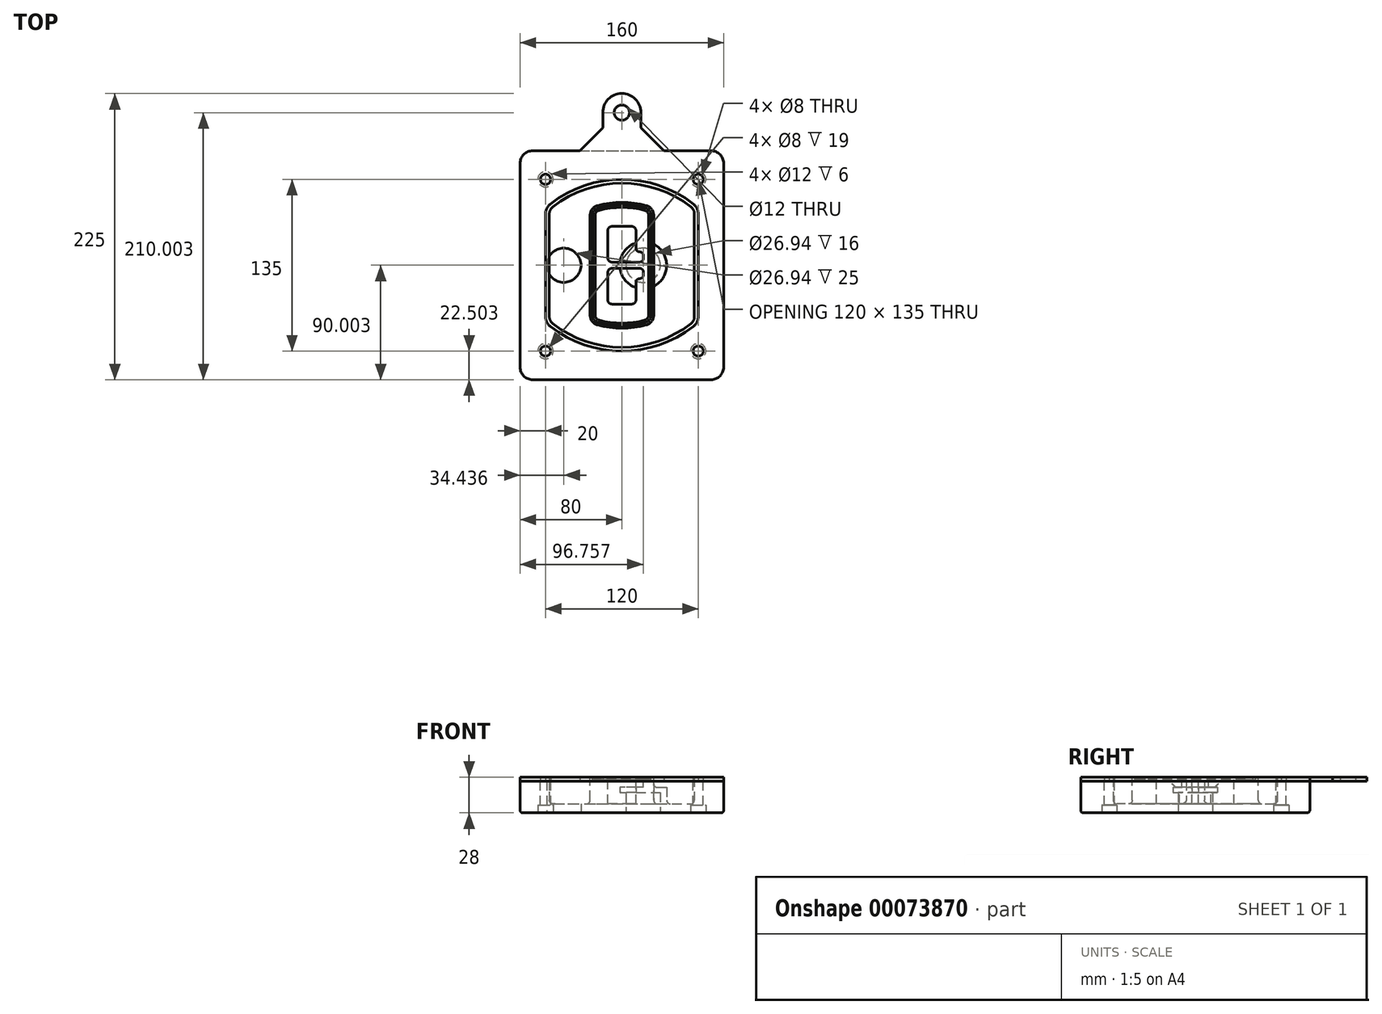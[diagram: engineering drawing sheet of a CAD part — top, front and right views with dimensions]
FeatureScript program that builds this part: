
annotation { "Feature Type Name" : "Feature", "Feature Type Description" : "" }
export const myFeature = defineFeature(function(context is Context, id is Id, definition is map)
    precondition{}
    {
        {
            var Q0;
            Q0=qCreatedBy(makeId("Top.planeOp"),FACE);
            var sketch = newSketch(context, id + "F0", { "sketchPlane" : qUnion([Q0])});
            skPoint(sketch, "E0.rect.middle", {"position": v(0, 0) * mm});
            skLineSegment(sketch, "E1.bottom", {"start": v(24.05, 28.38) * mm, "end": v(164.05, 28.38) * mm});
            skLineSegment(sketch, "E1.top", {"start": v(24.05, 208.38) * mm, "end": v(164.05, 208.38) * mm});
            skLineSegment(sketch, "E1.left", {"start": v(14.05, 38.38) * mm, "end": v(14.05, 198.38) * mm});
            skLineSegment(sketch, "E1.right", {"start": v(174.05, 38.38) * mm, "end": v(174.05, 198.38) * mm});
            skLineSegment(sketch, "E2", {"start": v(14.05, 208.38) * mm, "end": v(174.05, 28.38) * mm, "construction": true});
            skLineSegment(sketch, "E3", {"start": v(174.05, 208.38) * mm, "end": v(14.05, 28.38) * mm, "construction": true});
            skCircle(sketch, "E4", {"center": v(34.05, 185.88) * mm, "radius": 4 * mm});
            skCircle(sketch, "E5", {"center": v(154.05, 185.88) * mm, "radius": 4 * mm});
            skCircle(sketch, "E6", {"center": v(154.05, 50.88) * mm, "radius": 4 * mm});
            skCircle(sketch, "E7", {"center": v(34.05, 50.88) * mm, "radius": 4 * mm});
            skLineSegment(sketch, "E8", {"start": v(34.05, 185.88) * mm, "end": v(154.05, 185.88) * mm, "construction": true});
            skLineSegment(sketch, "E9", {"start": v(154.05, 185.88) * mm, "end": v(154.05, 50.88) * mm, "construction": true});
            skLineSegment(sketch, "E10", {"start": v(154.05, 50.88) * mm, "end": v(34.05, 50.88) * mm, "construction": true});
            skLineSegment(sketch, "E11", {"start": v(34.05, 50.88) * mm, "end": v(34.05, 185.88) * mm, "construction": true});
            skLineSegment(sketch, "E12", {"start": v(34.05, 158.68) * mm, "end": v(34.05, 78.09) * mm});
            skLineSegment(sketch, "E13", {"start": v(154.05, 158.68) * mm, "end": v(154.05, 78.09) * mm});
            skArc(sketch, "E14", {"start": v(150.2, 166.56) * mm, "mid": v(94.05, 185.88) * mm, "end": v(37.9, 166.56) * mm});
            skArc(sketch, "E15", {"start": v(37.9, 70.2) * mm, "mid": v(94.05, 50.88) * mm, "end": v(150.2, 70.2) * mm});
            skLineSegment(sketch, "E16", {"start": v(34.05, 118.38) * mm, "end": v(154.05, 118.38) * mm, "construction": true});
            skPoint(sketch, "E17.visualSharp", {"position": v(34.05, 73.38) * mm});
            skArc(sketch, "E17.filletArc", {"start": v(34.05, 78.09) * mm, "mid": v(35.06, 73.7) * mm, "end": v(37.9, 70.2) * mm});
            skPoint(sketch, "E18.visualSharp", {"position": v(34.05, 163.38) * mm});
            skArc(sketch, "E18.filletArc", {"start": v(37.9, 166.56) * mm, "mid": v(35.06, 163.06) * mm, "end": v(34.05, 158.68) * mm});
            skPoint(sketch, "E19.visualSharp", {"position": v(154.05, 163.38) * mm});
            skArc(sketch, "E19.filletArc", {"start": v(154.05, 158.68) * mm, "mid": v(153.04, 163.06) * mm, "end": v(150.2, 166.56) * mm});
            skPoint(sketch, "E20.visualSharp", {"position": v(154.05, 73.38) * mm});
            skArc(sketch, "E20.filletArc", {"start": v(150.2, 70.2) * mm, "mid": v(153.04, 73.7) * mm, "end": v(154.05, 78.09) * mm});
            skPoint(sketch, "E21.visualSharp", {"position": v(14.05, 208.38) * mm});
            skArc(sketch, "E21.filletArc", {"start": v(24.05, 208.38) * mm, "mid": v(16.98, 205.45) * mm, "end": v(14.05, 198.38) * mm});
            skPoint(sketch, "E22.visualSharp", {"position": v(174.05, 208.38) * mm});
            skArc(sketch, "E22.filletArc", {"start": v(174.05, 198.38) * mm, "mid": v(171.12, 205.45) * mm, "end": v(164.05, 208.38) * mm});
            skPoint(sketch, "E23.visualSharp", {"position": v(174.05, 28.38) * mm});
            skArc(sketch, "E23.filletArc", {"start": v(164.05, 28.38) * mm, "mid": v(171.12, 31.31) * mm, "end": v(174.05, 38.38) * mm});
            skPoint(sketch, "E24.visualSharp", {"position": v(14.05, 28.38) * mm});
            skArc(sketch, "E24.filletArc", {"start": v(14.05, 38.38) * mm, "mid": v(16.98, 31.31) * mm, "end": v(24.05, 28.38) * mm});
            skArc(sketch, "E25.0", {"start": v(151.05, 158.68) * mm, "mid": v(150.34, 161.75) * mm, "end": v(148.36, 164.2) * mm});
            skLineSegment(sketch, "E25.1", {"start": v(151.05, 158.68) * mm, "end": v(151.05, 78.09) * mm});
            skArc(sketch, "E25.2", {"start": v(148.36, 72.57) * mm, "mid": v(150.34, 75.02) * mm, "end": v(151.05, 78.09) * mm});
            skArc(sketch, "E25.3", {"start": v(39.74, 72.57) * mm, "mid": v(94.05, 53.88) * mm, "end": v(148.36, 72.57) * mm});
            skArc(sketch, "E25.4", {"start": v(37.05, 78.09) * mm, "mid": v(37.76, 75.02) * mm, "end": v(39.74, 72.57) * mm});
            skArc(sketch, "E25.5", {"start": v(148.36, 164.2) * mm, "mid": v(94.05, 182.88) * mm, "end": v(39.74, 164.2) * mm});
            skLineSegment(sketch, "E25.6", {"start": v(37.05, 158.68) * mm, "end": v(37.05, 78.09) * mm});
            skArc(sketch, "E25.7", {"start": v(39.74, 164.2) * mm, "mid": v(37.76, 161.75) * mm, "end": v(37.05, 158.68) * mm});
            skArc(sketch, "E26.0", {"start": v(35.43, 169.71) * mm, "mid": v(31.47, 164.82) * mm, "end": v(30.05, 158.68) * mm});
            skArc(sketch, "E26.1", {"start": v(152.67, 169.71) * mm, "mid": v(94.05, 189.88) * mm, "end": v(35.43, 169.71) * mm});
            skArc(sketch, "E26.2", {"start": v(158.05, 158.68) * mm, "mid": v(156.63, 164.82) * mm, "end": v(152.67, 169.71) * mm});
            skLineSegment(sketch, "E26.3", {"start": v(158.05, 158.68) * mm, "end": v(158.05, 78.09) * mm});
            skArc(sketch, "E26.4", {"start": v(152.67, 67.05) * mm, "mid": v(156.63, 71.95) * mm, "end": v(158.05, 78.09) * mm});
            skLineSegment(sketch, "E26.5", {"start": v(30.05, 158.68) * mm, "end": v(30.05, 78.09) * mm});
            skArc(sketch, "E26.6", {"start": v(35.43, 67.05) * mm, "mid": v(94.05, 46.88) * mm, "end": v(152.67, 67.05) * mm});
            skArc(sketch, "E26.7", {"start": v(30.05, 78.09) * mm, "mid": v(31.47, 71.95) * mm, "end": v(35.43, 67.05) * mm});
            skSolve(sketch);
        }
        {
            var Q0;
            Q0=makeQuery(id+"F0.imprint","IMPRINT",FACE,{"disambiguationData":[TD([[makeQuery(id+"F0.imprint","IMPRINT",EDGE,{"derivedFrom":sQuery(id+"F0.wireOp",EDGE,"E1.bottom")}),1.0]])]});
            var Q1;
            Q1=makeQuery(id+"F0.imprint","IMPRINT",FACE,{"disambiguationData":[TD([[makeQuery(id+"F0.imprint","IMPRINT",EDGE,{"derivedFrom":sQuery(id+"F0.wireOp",EDGE,"E12")}),1.0]])]});
            var Q2;
            Q2=makeQuery(id+"F0.imprint","IMPRINT",FACE,{"disambiguationData":[TD([[makeQuery(id+"F0.imprint","IMPRINT",EDGE,{"derivedFrom":sQuery(id+"F0.wireOp",EDGE,"E25.0")}),1.0]])]});
            var Q3;
            Q3=makeQuery(id+"F0.imprint","IMPRINT",FACE,{"disambiguationData":[TD([[makeQuery(id+"F0.imprint","IMPRINT",EDGE,{"derivedFrom":sQuery(id+"F0.wireOp",EDGE,"E12")}),-1.0]])]});
            extrude(context, id + "F1", {"entities" : qUnion([Q0, Q1, Q2, Q3]), "oppositeDirection" : true, "depth" : 25 * mm});
        }
        {
            var Q0;
            Q0=makeQuery(id+"F0.imprint","IMPRINT",FACE,{"disambiguationData":[TD([[makeQuery(id+"F0.imprint","IMPRINT",EDGE,{"derivedFrom":sQuery(id+"F0.wireOp",EDGE,"E12")}),1.0]])]});
            extrude(context, id + "F2", {"entities" : qUnion([Q0]), "operationType" : NewBodyOperationType.ADD, "depth" : 3 * mm});
        }
        {
            var Q0;
            Q0=makeQuery(id+"F0.imprint","IMPRINT",FACE,{"disambiguationData":[TD([[makeQuery(id+"F0.imprint","IMPRINT",EDGE,{"derivedFrom":sQuery(id+"F0.wireOp",EDGE,"E25.0")}),1.0]])]});
            extrude(context, id + "F3", {"entities" : qUnion([Q0]), "operationType" : NewBodyOperationType.REMOVE, "oppositeDirection" : true, "depth" : 18 * mm});
        }
        {
            var Q0;
            Q0=makeQuery(id+"F2.opExtrude","CAP_FACE",FACE,{"disambiguationData":[OSD([sQuery(id+"F0.wireOp",EDGE,"E12"),sQuery(id+"F0.wireOp",EDGE,"E13"),sQuery(id+"F0.wireOp",EDGE,"E14"),sQuery(id+"F0.wireOp",EDGE,"E15"),sQuery(id+"F0.wireOp",EDGE,"E17.filletArc"),sQuery(id+"F0.wireOp",EDGE,"E18.filletArc"),sQuery(id+"F0.wireOp",EDGE,"E19.filletArc"),sQuery(id+"F0.wireOp",EDGE,"E20.filletArc"),sQuery(id+"F0.wireOp",EDGE,"E25.0"),sQuery(id+"F0.wireOp",EDGE,"E25.1"),sQuery(id+"F0.wireOp",EDGE,"E25.2"),sQuery(id+"F0.wireOp",EDGE,"E25.3"),sQuery(id+"F0.wireOp",EDGE,"E25.4"),sQuery(id+"F0.wireOp",EDGE,"E25.5"),sQuery(id+"F0.wireOp",EDGE,"E25.6"),sQuery(id+"F0.wireOp",EDGE,"E25.7")])],"isStart":false});
            var sketch = newSketch(context, id + "F4", { "sketchPlane" : qUnion([Q0])});
            skArc(sketch, "E27.0", {"start": v(74.97, 71.41) * mm, "mid": v(94.05, 68.88) * mm, "end": v(113.13, 71.41) * mm});
            skArc(sketch, "E28.0", {"start": v(113.13, 165.35) * mm, "mid": v(94.05, 167.88) * mm, "end": v(74.97, 165.35) * mm});
            skLineSegment(sketch, "E29", {"start": v(69.05, 157.63) * mm, "end": v(69.05, 79.14) * mm});
            skLineSegment(sketch, "E30", {"start": v(119.05, 157.63) * mm, "end": v(119.05, 79.14) * mm});
            skLineSegment(sketch, "E31", {"start": v(69.05, 163.48) * mm, "end": v(119.05, 163.48) * mm, "construction": true});
            skLineSegment(sketch, "E32", {"start": v(69.05, 73.28) * mm, "end": v(119.05, 73.28) * mm, "construction": true});
            skPoint(sketch, "E33.visualSharp", {"position": v(69.05, 163.48) * mm});
            skArc(sketch, "E33.filletArc", {"start": v(74.97, 165.35) * mm, "mid": v(70.7, 162.5) * mm, "end": v(69.05, 157.63) * mm});
            skPoint(sketch, "E34.visualSharp", {"position": v(119.05, 163.48) * mm});
            skArc(sketch, "E34.filletArc", {"start": v(119.05, 157.63) * mm, "mid": v(117.4, 162.5) * mm, "end": v(113.13, 165.35) * mm});
            skPoint(sketch, "E35.visualSharp", {"position": v(119.05, 73.28) * mm});
            skArc(sketch, "E35.filletArc", {"start": v(113.13, 71.41) * mm, "mid": v(117.4, 74.27) * mm, "end": v(119.05, 79.14) * mm});
            skPoint(sketch, "E36.visualSharp", {"position": v(69.05, 73.28) * mm});
            skArc(sketch, "E36.filletArc", {"start": v(69.05, 79.14) * mm, "mid": v(70.7, 74.27) * mm, "end": v(74.97, 71.41) * mm});
            skArc(sketch, "E37.0", {"start": v(148.36, 164.2) * mm, "mid": v(94.05, 182.88) * mm, "end": v(39.74, 164.2) * mm});
            skArc(sketch, "E37.1", {"start": v(39.74, 164.2) * mm, "mid": v(37.76, 161.75) * mm, "end": v(37.05, 158.68) * mm});
            skLineSegment(sketch, "E37.2", {"start": v(37.05, 158.68) * mm, "end": v(37.05, 78.09) * mm});
            skArc(sketch, "E37.3", {"start": v(37.05, 78.09) * mm, "mid": v(37.76, 75.02) * mm, "end": v(39.74, 72.57) * mm});
            skArc(sketch, "E37.4", {"start": v(39.74, 72.57) * mm, "mid": v(94.05, 53.88) * mm, "end": v(148.36, 72.57) * mm});
            skArc(sketch, "E37.5", {"start": v(148.36, 72.57) * mm, "mid": v(150.34, 75.02) * mm, "end": v(151.05, 78.09) * mm});
            skLineSegment(sketch, "E37.6", {"start": v(151.05, 158.68) * mm, "end": v(151.05, 78.09) * mm});
            skArc(sketch, "E37.7", {"start": v(151.05, 158.68) * mm, "mid": v(150.34, 161.75) * mm, "end": v(148.36, 164.2) * mm});
            skLineSegment(sketch, "E38.0", {"start": v(117.05, 157.63) * mm, "end": v(117.05, 79.14) * mm});
            skArc(sketch, "E38.1", {"start": v(112.61, 73.34) * mm, "mid": v(115.81, 75.49) * mm, "end": v(117.05, 79.14) * mm});
            skArc(sketch, "E38.2", {"start": v(75.49, 73.34) * mm, "mid": v(94.05, 70.88) * mm, "end": v(112.61, 73.34) * mm});
            skArc(sketch, "E38.3", {"start": v(71.05, 79.14) * mm, "mid": v(72.29, 75.49) * mm, "end": v(75.49, 73.34) * mm});
            skLineSegment(sketch, "E38.4", {"start": v(71.05, 157.63) * mm, "end": v(71.05, 79.14) * mm});
            skArc(sketch, "E38.5", {"start": v(117.05, 157.63) * mm, "mid": v(115.81, 161.28) * mm, "end": v(112.61, 163.42) * mm});
            skArc(sketch, "E38.6", {"start": v(75.49, 163.42) * mm, "mid": v(72.29, 161.28) * mm, "end": v(71.05, 157.63) * mm});
            skArc(sketch, "E38.7", {"start": v(112.61, 163.42) * mm, "mid": v(94.05, 165.88) * mm, "end": v(75.49, 163.42) * mm});
            skArc(sketch, "E39.0", {"start": v(115.05, 157.63) * mm, "mid": v(114.23, 160.06) * mm, "end": v(112.1, 161.5) * mm});
            skLineSegment(sketch, "E39.1", {"start": v(115.05, 157.63) * mm, "end": v(115.05, 79.14) * mm});
            skArc(sketch, "E39.2", {"start": v(112.1, 75.27) * mm, "mid": v(114.23, 76.7) * mm, "end": v(115.05, 79.14) * mm});
            skArc(sketch, "E39.3", {"start": v(76, 75.27) * mm, "mid": v(94.05, 72.88) * mm, "end": v(112.1, 75.27) * mm});
            skArc(sketch, "E39.4", {"start": v(73.05, 79.14) * mm, "mid": v(73.87, 76.7) * mm, "end": v(76, 75.27) * mm});
            skArc(sketch, "E39.5", {"start": v(112.1, 161.5) * mm, "mid": v(94.05, 163.88) * mm, "end": v(76, 161.5) * mm});
            skLineSegment(sketch, "E39.6", {"start": v(73.05, 157.63) * mm, "end": v(73.05, 79.14) * mm});
            skArc(sketch, "E39.7", {"start": v(76, 161.5) * mm, "mid": v(73.87, 160.06) * mm, "end": v(73.05, 157.63) * mm});
            skLineSegment(sketch, "E40", {"start": v(69.05, 118.38) * mm, "end": v(119.05, 118.38) * mm, "construction": true});
            skLineSegment(sketch, "E41", {"start": v(83.05, 123.88) * mm, "end": v(83.05, 145.88) * mm});
            skLineSegment(sketch, "E42", {"start": v(86.05, 148.88) * mm, "end": v(102.05, 148.88) * mm});
            skLineSegment(sketch, "E43", {"start": v(105.05, 145.88) * mm, "end": v(105.05, 131.88) * mm});
            skLineSegment(sketch, "E44", {"start": v(108.05, 128.88) * mm, "end": v(108.05, 128.88) * mm});
            skLineSegment(sketch, "E45", {"start": v(111.05, 125.88) * mm, "end": v(111.05, 123.88) * mm});
            skLineSegment(sketch, "E46", {"start": v(108.05, 120.88) * mm, "end": v(86.05, 120.88) * mm});
            skPoint(sketch, "E47.visualSharp", {"position": v(83.05, 148.88) * mm});
            skArc(sketch, "E47.filletArc", {"start": v(86.05, 148.88) * mm, "mid": v(83.93, 148) * mm, "end": v(83.05, 145.88) * mm});
            skPoint(sketch, "E48.visualSharp", {"position": v(105.05, 148.88) * mm});
            skArc(sketch, "E48.filletArc", {"start": v(105.05, 145.88) * mm, "mid": v(104.17, 148) * mm, "end": v(102.05, 148.88) * mm});
            skPoint(sketch, "E49.visualSharp", {"position": v(105.05, 128.88) * mm});
            skArc(sketch, "E49.filletArc", {"start": v(105.05, 131.88) * mm, "mid": v(105.93, 129.76) * mm, "end": v(108.05, 128.88) * mm});
            skPoint(sketch, "E50.visualSharp", {"position": v(111.05, 128.88) * mm});
            skArc(sketch, "E50.filletArc", {"start": v(111.05, 125.88) * mm, "mid": v(110.17, 128) * mm, "end": v(108.05, 128.88) * mm});
            skPoint(sketch, "E51.visualSharp", {"position": v(111.05, 120.88) * mm});
            skArc(sketch, "E51.filletArc", {"start": v(108.05, 120.88) * mm, "mid": v(110.17, 121.76) * mm, "end": v(111.05, 123.88) * mm});
            skPoint(sketch, "E52.visualSharp", {"position": v(83.05, 120.88) * mm});
            skArc(sketch, "E52.filletArc", {"start": v(83.05, 123.88) * mm, "mid": v(83.93, 121.76) * mm, "end": v(86.05, 120.88) * mm});
            skLineSegment(sketch, "E53.0.MirrorCS", {"start": v(108.05, 115.88) * mm, "end": v(86.05, 115.88) * mm});
            skArc(sketch, "E54.0.MirrorCS", {"start": v(83.05, 112.88) * mm, "mid": v(83.93, 115) * mm, "end": v(86.05, 115.88) * mm});
            skLineSegment(sketch, "E55.0.MirrorCS", {"start": v(83.05, 112.88) * mm, "end": v(83.05, 90.88) * mm});
            skArc(sketch, "E56.0.MirrorCS", {"start": v(86.05, 87.88) * mm, "mid": v(83.93, 88.76) * mm, "end": v(83.05, 90.88) * mm});
            skLineSegment(sketch, "E57.0.MirrorCS", {"start": v(86.05, 87.88) * mm, "end": v(102.05, 87.88) * mm});
            skArc(sketch, "E58.0.MirrorCS", {"start": v(105.05, 90.88) * mm, "mid": v(104.17, 88.76) * mm, "end": v(102.05, 87.88) * mm});
            skLineSegment(sketch, "E59.0.MirrorCS", {"start": v(105.05, 90.88) * mm, "end": v(105.05, 104.88) * mm});
            skArc(sketch, "E60.0.MirrorCS", {"start": v(105.05, 104.88) * mm, "mid": v(105.93, 107) * mm, "end": v(108.05, 107.88) * mm});
            skArc(sketch, "E61.0.MirrorCS", {"start": v(111.05, 110.88) * mm, "mid": v(110.17, 108.76) * mm, "end": v(108.05, 107.88) * mm});
            skLineSegment(sketch, "E62.0.MirrorCS", {"start": v(111.05, 110.88) * mm, "end": v(111.05, 112.88) * mm});
            skArc(sketch, "E63.0.MirrorCS", {"start": v(108.05, 115.88) * mm, "mid": v(110.17, 115) * mm, "end": v(111.05, 112.88) * mm});
            skSolve(sketch);
        }
        {
            var Q0;
            Q0=makeQuery(id+"F4.imprint","IMPRINT",FACE,{"disambiguationData":[TD([[makeQuery(id+"F4.imprint","IMPRINT",EDGE,{"derivedFrom":sQuery(id+"F4.wireOp",EDGE,"E27.0")}),1.0]])]});
            var Q1;
            Q1=makeQuery(id+"F4.imprint","IMPRINT",FACE,{"disambiguationData":[TD([[makeQuery(id+"F4.imprint","IMPRINT",EDGE,{"derivedFrom":sQuery(id+"F4.wireOp",EDGE,"E38.0")}),-1.0]])]});
            var Q2;
            Q2=makeQuery(id+"F4.imprint","IMPRINT",FACE,{"disambiguationData":[TD([[makeQuery(id+"F4.imprint","IMPRINT",EDGE,{"derivedFrom":sQuery(id+"F4.wireOp",EDGE,"E39.0")}),1.0]])]});
            extrude(context, id + "F5", {"entities" : qUnion([Q0, Q1, Q2]), "operationType" : NewBodyOperationType.ADD, "endBound" : BoundingType.UP_TO_NEXT, "oppositeDirection" : true, "depth" : 25 * mm});
        }
        {
            var Q0;
            Q0=makeQuery(id+"F4.imprint","IMPRINT",FACE,{"disambiguationData":[TD([[makeQuery(id+"F4.imprint","IMPRINT",EDGE,{"derivedFrom":sQuery(id+"F4.wireOp",EDGE,"E38.0")}),-1.0]])]});
            extrude(context, id + "F6", {"entities" : qUnion([Q0]), "operationType" : NewBodyOperationType.REMOVE, "oppositeDirection" : true, "depth" : 2 * mm});
        }
        {
            var Q0;
            Q0=makeQuery(id+"F1.opExtrude","CAP_FACE",FACE,{"disambiguationData":[OSD([sQuery(id+"F0.wireOp",EDGE,"E1.bottom"),sQuery(id+"F0.wireOp",EDGE,"E1.top"),sQuery(id+"F0.wireOp",EDGE,"E1.left"),sQuery(id+"F0.wireOp",EDGE,"E1.right"),sQuery(id+"F0.wireOp",EDGE,"E4"),sQuery(id+"F0.wireOp",EDGE,"E5"),sQuery(id+"F0.wireOp",EDGE,"E6"),sQuery(id+"F0.wireOp",EDGE,"E7"),sQuery(id+"F0.wireOp",EDGE,"E21.filletArc"),sQuery(id+"F0.wireOp",EDGE,"E22.filletArc"),sQuery(id+"F0.wireOp",EDGE,"E23.filletArc"),sQuery(id+"F0.wireOp",EDGE,"E24.filletArc")])],"isStart":false});
            var sketch = newSketch(context, id + "F7", { "sketchPlane" : qUnion([Q0])});
            skCircle(sketch, "E64", {"center": v(110.8, -118.38) * mm, "radius": 13.47 * mm});
            skCircle(sketch, "E65", {"center": v(48.49, -118.38) * mm, "radius": 13.47 * mm});
            skLineSegment(sketch, "E66", {"start": v(174.05, -118.38) * mm, "end": v(14.05, -118.38) * mm});
            skCircle(sketch, "E67", {"center": v(110.8, -118.38) * mm, "radius": 18.47 * mm});
            skCircle(sketch, "E68", {"center": v(154.05, -185.88) * mm, "radius": 6 * mm});
            skCircle(sketch, "E69", {"center": v(34.05, -185.88) * mm, "radius": 6 * mm});
            skCircle(sketch, "E70", {"center": v(34.05, -50.88) * mm, "radius": 6 * mm});
            skCircle(sketch, "E71", {"center": v(154.05, -50.88) * mm, "radius": 6 * mm});
            skSolve(sketch);
        }
        {
            var Q0;
            {var subQ1=sQuery(id+"F7.wireOp",EDGE,"E66");var subQ4=sQuery(id+"F7.wireOp",EDGE,"E64");var subQ6=makeQuery(id+"F7.imprint","INTERSECT",VERTEX,{"disambiguationData":[OD(0.0)],"derivedFrom":[subQ4,subQ1]});Q0=makeQuery(id+"F7.imprint","IMPRINT",FACE,{"disambiguationData":[TD([[makeQuery(id+"F7.imprint","IMPRINT",EDGE,{"disambiguationData":[TD([[subQ6,-1.0]])],"derivedFrom":subQ4}),-1.0]])]});}
            var Q1;
            {var subQ0=sQuery(id+"F7.wireOp",EDGE,"E66");var subQ1=sQuery(id+"F7.wireOp",EDGE,"E64");var subQ3=makeQuery(id+"F7.imprint","INTERSECT",VERTEX,{"disambiguationData":[OD(0.0)],"derivedFrom":[subQ1,subQ0]});Q1=makeQuery(id+"F7.imprint","IMPRINT",FACE,{"disambiguationData":[TD([[makeQuery(id+"F7.imprint","IMPRINT",EDGE,{"disambiguationData":[TD([[subQ3,-1.0]])],"derivedFrom":subQ1}),1.0]])]});}
            var Q2;
            {var subQ0=sQuery(id+"F7.wireOp",EDGE,"E66");var subQ1=sQuery(id+"F7.wireOp",EDGE,"E64");var subQ3=makeQuery(id+"F7.imprint","INTERSECT",VERTEX,{"disambiguationData":[OD(0.0)],"derivedFrom":[subQ1,subQ0]});Q2=makeQuery(id+"F7.imprint","IMPRINT",FACE,{"disambiguationData":[TD([[makeQuery(id+"F7.imprint","IMPRINT",EDGE,{"disambiguationData":[TD([[subQ3,1.0]])],"derivedFrom":subQ1}),1.0]])]});}
            var Q3;
            {var subQ1=sQuery(id+"F7.wireOp",EDGE,"E66");var subQ4=sQuery(id+"F7.wireOp",EDGE,"E64");var subQ6=makeQuery(id+"F7.imprint","INTERSECT",VERTEX,{"disambiguationData":[OD(0.0)],"derivedFrom":[subQ4,subQ1]});Q3=makeQuery(id+"F7.imprint","IMPRINT",FACE,{"disambiguationData":[TD([[makeQuery(id+"F7.imprint","IMPRINT",EDGE,{"disambiguationData":[TD([[subQ6,1.0]])],"derivedFrom":subQ4}),-1.0]])]});}
            extrude(context, id + "F8", {"entities" : qUnion([Q0, Q1, Q2, Q3]), "operationType" : NewBodyOperationType.ADD, "oppositeDirection" : true, "depth" : 20 * mm});
        }
        {
            var Q0;
            {var subQ0=sQuery(id+"F7.wireOp",EDGE,"E66");var subQ1=sQuery(id+"F7.wireOp",EDGE,"E64");var subQ3=makeQuery(id+"F7.imprint","INTERSECT",VERTEX,{"disambiguationData":[OD(0.0)],"derivedFrom":[subQ1,subQ0]});Q0=makeQuery(id+"F7.imprint","IMPRINT",FACE,{"disambiguationData":[TD([[makeQuery(id+"F7.imprint","IMPRINT",EDGE,{"disambiguationData":[TD([[subQ3,-1.0]])],"derivedFrom":subQ1}),1.0]])]});}
            var Q1;
            {var subQ0=sQuery(id+"F7.wireOp",EDGE,"E66");var subQ1=sQuery(id+"F7.wireOp",EDGE,"E64");var subQ3=makeQuery(id+"F7.imprint","INTERSECT",VERTEX,{"disambiguationData":[OD(0.0)],"derivedFrom":[subQ1,subQ0]});Q1=makeQuery(id+"F7.imprint","IMPRINT",FACE,{"disambiguationData":[TD([[makeQuery(id+"F7.imprint","IMPRINT",EDGE,{"disambiguationData":[TD([[subQ3,1.0]])],"derivedFrom":subQ1}),1.0]])]});}
            extrude(context, id + "F9", {"entities" : qUnion([Q0, Q1]), "operationType" : NewBodyOperationType.REMOVE, "oppositeDirection" : true, "depth" : 16 * mm});
        }
        {
            var Q0;
            {var subQ0=sQuery(id+"F7.wireOp",EDGE,"E66");var subQ1=sQuery(id+"F7.wireOp",EDGE,"E65");var subQ3=makeQuery(id+"F7.imprint","INTERSECT",VERTEX,{"disambiguationData":[OD(0.0)],"derivedFrom":[subQ1,subQ0]});Q0=makeQuery(id+"F7.imprint","IMPRINT",FACE,{"disambiguationData":[TD([[makeQuery(id+"F7.imprint","IMPRINT",EDGE,{"disambiguationData":[TD([[subQ3,-1.0]])],"derivedFrom":subQ1}),1.0]])]});}
            var Q1;
            {var subQ0=sQuery(id+"F7.wireOp",EDGE,"E66");var subQ1=sQuery(id+"F7.wireOp",EDGE,"E65");var subQ3=makeQuery(id+"F7.imprint","INTERSECT",VERTEX,{"disambiguationData":[OD(0.0)],"derivedFrom":[subQ1,subQ0]});Q1=makeQuery(id+"F7.imprint","IMPRINT",FACE,{"disambiguationData":[TD([[makeQuery(id+"F7.imprint","IMPRINT",EDGE,{"disambiguationData":[TD([[subQ3,1.0]])],"derivedFrom":subQ1}),1.0]])]});}
            extrude(context, id + "F10", {"entities" : qUnion([Q0, Q1]), "operationType" : NewBodyOperationType.REMOVE, "oppositeDirection" : true, "depth" : 25 * mm});
        }
        {
            var Q0;
            Q0=makeQuery(id+"F7.imprint","IMPRINT",FACE,{"disambiguationData":[TD([[makeQuery(id+"F7.imprint","IMPRINT",EDGE,{"derivedFrom":sQuery(id+"F7.wireOp",EDGE,"E68")}),1.0]])]});
            var Q1;
            Q1=makeQuery(id+"F7.imprint","IMPRINT",FACE,{"disambiguationData":[TD([[makeQuery(id+"F7.imprint","IMPRINT",EDGE,{"derivedFrom":makeQuery(id+"F1.opExtrude","CAP_EDGE",EDGE,{"disambiguationData":[OSD([sQuery(id+"F0.wireOp",EDGE,"E5")])],"isStart":false})}),-1.0]])]});
            var Q2;
            Q2=makeQuery(id+"F7.imprint","IMPRINT",FACE,{"disambiguationData":[TD([[makeQuery(id+"F7.imprint","IMPRINT",EDGE,{"derivedFrom":sQuery(id+"F7.wireOp",EDGE,"E69")}),1.0]])]});
            var Q3;
            Q3=makeQuery(id+"F7.imprint","IMPRINT",FACE,{"disambiguationData":[TD([[makeQuery(id+"F7.imprint","IMPRINT",EDGE,{"derivedFrom":makeQuery(id+"F1.opExtrude","CAP_EDGE",EDGE,{"disambiguationData":[OSD([sQuery(id+"F0.wireOp",EDGE,"E4")])],"isStart":false})}),-1.0]])]});
            var Q4;
            Q4=makeQuery(id+"F7.imprint","IMPRINT",FACE,{"disambiguationData":[TD([[makeQuery(id+"F7.imprint","IMPRINT",EDGE,{"derivedFrom":sQuery(id+"F7.wireOp",EDGE,"E70")}),1.0]])]});
            var Q5;
            Q5=makeQuery(id+"F7.imprint","IMPRINT",FACE,{"disambiguationData":[TD([[makeQuery(id+"F7.imprint","IMPRINT",EDGE,{"derivedFrom":makeQuery(id+"F1.opExtrude","CAP_EDGE",EDGE,{"disambiguationData":[OSD([sQuery(id+"F0.wireOp",EDGE,"E7")])],"isStart":false})}),-1.0]])]});
            var Q6;
            Q6=makeQuery(id+"F7.imprint","IMPRINT",FACE,{"disambiguationData":[TD([[makeQuery(id+"F7.imprint","IMPRINT",EDGE,{"derivedFrom":sQuery(id+"F7.wireOp",EDGE,"E71")}),1.0]])]});
            var Q7;
            Q7=makeQuery(id+"F7.imprint","IMPRINT",FACE,{"disambiguationData":[TD([[makeQuery(id+"F7.imprint","IMPRINT",EDGE,{"derivedFrom":makeQuery(id+"F1.opExtrude","CAP_EDGE",EDGE,{"disambiguationData":[OSD([sQuery(id+"F0.wireOp",EDGE,"E6")])],"isStart":false})}),-1.0]])]});
            extrude(context, id + "F11", {"entities" : qUnion([Q0, Q1, Q2, Q3, Q4, Q5, Q6, Q7]), "operationType" : NewBodyOperationType.REMOVE, "oppositeDirection" : true, "depth" : 6 * mm});
        }
        {
            var Q0;
            Q0=makeQuery(id+"F9.boolean.opBoolean","COPY",FACE,{"derivedFrom":makeQuery(id+"F9.opExtrude","CAP_FACE",FACE,{"disambiguationData":[OSD([sQuery(id+"F7.wireOp",EDGE,"E64")])],"isStart":false})});
            var sketch = newSketch(context, id + "F12", { "sketchPlane" : qUnion([Q0])});
            skArc(sketch, "E72.0", {"start": v(105.05, -100.83) * mm, "mid": v(96.62, -106.56) * mm, "end": v(92.5, -115.88) * mm});
            skArc(sketch, "E72.1", {"start": v(92.5, -120.88) * mm, "mid": v(96.62, -130.2) * mm, "end": v(105.05, -135.93) * mm});
            skLineSegment(sketch, "E73", {"start": v(92.5, -120.88) * mm, "end": v(108.05, -120.88) * mm});
            skLineSegment(sketch, "E74.0", {"start": v(108.05, -115.88) * mm, "end": v(92.5, -115.88) * mm});
            skArc(sketch, "E74.1", {"start": v(108.05, -115.88) * mm, "mid": v(110.17, -115) * mm, "end": v(111.05, -112.88) * mm});
            skLineSegment(sketch, "E74.2", {"start": v(111.05, -110.88) * mm, "end": v(111.05, -112.88) * mm});
            skArc(sketch, "E74.3", {"start": v(111.05, -110.88) * mm, "mid": v(110.17, -108.76) * mm, "end": v(108.05, -107.88) * mm});
            skArc(sketch, "E74.4", {"start": v(105.05, -104.88) * mm, "mid": v(105.93, -107) * mm, "end": v(108.05, -107.88) * mm});
            skLineSegment(sketch, "E74.5", {"start": v(105.05, -100.83) * mm, "end": v(105.05, -104.88) * mm});
            skLineSegment(sketch, "E74.7", {"start": v(108.05, -120.88) * mm, "end": v(92.5, -120.88) * mm});
            skArc(sketch, "E74.8", {"start": v(108.05, -120.88) * mm, "mid": v(110.17, -121.76) * mm, "end": v(111.05, -123.88) * mm});
            skLineSegment(sketch, "E74.9", {"start": v(111.05, -125.88) * mm, "end": v(111.05, -123.88) * mm});
            skArc(sketch, "E74.10", {"start": v(111.05, -125.88) * mm, "mid": v(110.17, -128) * mm, "end": v(108.05, -128.88) * mm});
            skArc(sketch, "E74.11", {"start": v(105.05, -131.88) * mm, "mid": v(105.93, -129.76) * mm, "end": v(108.05, -128.88) * mm});
            skLineSegment(sketch, "E74.12", {"start": v(105.05, -135.93) * mm, "end": v(105.05, -131.88) * mm});
            skPoint(sketch, "E75.orphan", {"position": v(105.05, -145.88) * mm});
            skPoint(sketch, "E76.orphan", {"position": v(86.05, -120.88) * mm});
            skPoint(sketch, "E77.orphan", {"position": v(86.05, -115.88) * mm});
            skPoint(sketch, "E78.orphan", {"position": v(105.05, -90.88) * mm});
            skSolve(sketch);
        }
        {
            var Q0;
            {var subQ7=sQuery(id+"F12.wireOp",EDGE,"E72.0");var subQ14=sQuery(id+"F12.wireOp",EDGE,"E72.1");var subQ16=sQuery(id+"F12.wireOp",EDGE,"E74.1");var subQ18=sQuery(id+"F12.wireOp",EDGE,"E74.8");Q0=qUnion([makeQuery(id+"F12.imprint","IMPRINT",FACE,{"disambiguationData":[TD([[makeQuery(id+"F12.imprint","IMPRINT",EDGE,{"derivedFrom":subQ7}),1.0]])]}),makeQuery(id+"F12.imprint","IMPRINT",FACE,{"disambiguationData":[TD([[makeQuery(id+"F12.imprint","IMPRINT",EDGE,{"derivedFrom":subQ14}),1.0]])]}),makeQuery(id+"F12.imprint","IMPRINT",FACE,{"disambiguationData":[TD([[makeQuery(id+"F12.imprint","IMPRINT",EDGE,{"derivedFrom":subQ16}),1.0]])]}),makeQuery(id+"F12.imprint","IMPRINT",FACE,{"disambiguationData":[TD([[makeQuery(id+"F12.imprint","IMPRINT",EDGE,{"derivedFrom":subQ18}),-1.0]])]})]);}
            var Q1;
            Q1=makeQuery(id+"F5.boolean.opBoolean","SPLIT",FACE,{"disambiguationData":[TD([makeQuery(id+"F5.opExtrude","SWEPT_FACE",FACE,{"disambiguationData":[OSD([sQuery(id+"F4.wireOp",EDGE,"E41")])]})])],"derivedFrom":makeQuery(id+"F3.boolean.opBoolean","COPY",FACE,{"derivedFrom":makeQuery(id+"F3.opExtrude","CAP_FACE",FACE,{"disambiguationData":[OSD([sQuery(id+"F0.wireOp",EDGE,"E25.0"),sQuery(id+"F0.wireOp",EDGE,"E25.1"),sQuery(id+"F0.wireOp",EDGE,"E25.2"),sQuery(id+"F0.wireOp",EDGE,"E25.3"),sQuery(id+"F0.wireOp",EDGE,"E25.4"),sQuery(id+"F0.wireOp",EDGE,"E25.5"),sQuery(id+"F0.wireOp",EDGE,"E25.6"),sQuery(id+"F0.wireOp",EDGE,"E25.7")])],"isStart":false})})});
            extrude(context, id + "F13", {"entities" : qUnion([Q0]), "operationType" : NewBodyOperationType.REMOVE, "endBound" : BoundingType.UP_TO_SURFACE, "endBoundEntityFace" : qUnion([Q1]), "depth" : 25 * mm});
        }
        {
            var Q0;
            Q0=makeQuery(id+"F3.boolean.opBoolean","COPY",EDGE,{"derivedFrom":makeQuery(id+"F3.opExtrude","CAP_EDGE",EDGE,{"disambiguationData":[OSD([sQuery(id+"F0.wireOp",EDGE,"E25.6")])],"isStart":false})});
            var Q1;
            Q1=makeQuery(id+"F8.boolean.opBoolean","INTERSECT",EDGE,{"derivedFrom":[makeQuery(id+"F5.opExtrude","SWEPT_FACE",FACE,{"disambiguationData":[OSD([sQuery(id+"F4.wireOp",EDGE,"E30")])]}),makeQuery(id+"F8.opExtrude","CAP_FACE",FACE,{"disambiguationData":[OSD([sQuery(id+"F7.wireOp",EDGE,"E67")])],"isStart":false})]});
            var Q2;
            Q2=makeQuery(id+"F8.boolean.opBoolean","INTERSECT",EDGE,{"disambiguationData":[OD(1.0)],"derivedFrom":[makeQuery(id+"F5.opExtrude","SWEPT_FACE",FACE,{"disambiguationData":[OSD([sQuery(id+"F4.wireOp",EDGE,"E30")])]}),makeQuery(id+"F8.opExtrude","SWEPT_FACE",FACE,{"disambiguationData":[OSD([sQuery(id+"F7.wireOp",EDGE,"E67")])]})]});
            var Q3;
            {var subQ0=sQuery(id+"F4.wireOp",EDGE,"E30");Q3=makeQuery(id+"F8.boolean.opBoolean","SPLIT",EDGE,{"disambiguationData":[TD([makeQuery(id+"F5.opExtrude","SWEPT_FACE",FACE,{"disambiguationData":[OSD([sQuery(id+"F4.wireOp",EDGE,"E35.filletArc")])]})])],"derivedFrom":makeQuery(id+"F5.opExtrude","CAP_EDGE",EDGE,{"disambiguationData":[OSD([subQ0])],"isStart":false})});}
            var Q4;
            {var subQ0=sQuery(id+"F0.wireOp",EDGE,"E25.7");var subQ1=sQuery(id+"F0.wireOp",EDGE,"E25.1");var subQ2=sQuery(id+"F0.wireOp",EDGE,"E25.6");var subQ3=sQuery(id+"F0.wireOp",EDGE,"E25.5");var subQ4=sQuery(id+"F0.wireOp",EDGE,"E25.4");var subQ5=sQuery(id+"F0.wireOp",EDGE,"E25.0");var subQ6=sQuery(id+"F0.wireOp",EDGE,"E25.2");var subQ7=sQuery(id+"F0.wireOp",EDGE,"E25.3");Q4=makeQuery(id+"F8.boolean.opBoolean","INTERSECT",EDGE,{"derivedFrom":[makeQuery(id+"F5.boolean.opBoolean","SPLIT",FACE,{"disambiguationData":[TD([makeQuery(id+"F2.opExtrude","SWEPT_FACE",FACE,{"disambiguationData":[OSD([subQ5])]})])],"derivedFrom":makeQuery(id+"F3.boolean.opBoolean","COPY",FACE,{"derivedFrom":makeQuery(id+"F3.opExtrude","CAP_FACE",FACE,{"disambiguationData":[OSD([subQ5,subQ1,subQ6,subQ7,subQ4,subQ3,subQ2,subQ0])],"isStart":false})})}),makeQuery(id+"F8.opExtrude","SWEPT_FACE",FACE,{"disambiguationData":[OSD([sQuery(id+"F7.wireOp",EDGE,"E67")])]})]});}
            var Q5;
            Q5=makeQuery(id+"F8.boolean.opBoolean","INTERSECT",EDGE,{"disambiguationData":[OD(0.0)],"derivedFrom":[makeQuery(id+"F5.opExtrude","SWEPT_FACE",FACE,{"disambiguationData":[OSD([sQuery(id+"F4.wireOp",EDGE,"E30")])]}),makeQuery(id+"F8.opExtrude","SWEPT_FACE",FACE,{"disambiguationData":[OSD([sQuery(id+"F7.wireOp",EDGE,"E67")])]})]});
            fillet(context, id + "F14", {"entities" : qUnion([Q0, Q1, Q2, Q3, Q4, Q5]), "radius" : 3 * mm, "tangentPropagation" : true, "allowEdgeOverflow" : false});
        }
        {
            var Q0;
            Q0=makeQuery(id+"F1.opExtrude","CAP_EDGE",EDGE,{"disambiguationData":[OSD([sQuery(id+"F0.wireOp",EDGE,"E1.bottom")])],"isStart":false});
            fillet(context, id + "F15", {"entities" : qUnion([Q0]), "radius" : 2 * mm, "tangentPropagation" : true, "allowEdgeOverflow" : false});
        }
        {
            var Q0;
            {var subQ0=sQuery(id+"F0.wireOp",EDGE,"E22.filletArc");var subQ1=sQuery(id+"F0.wireOp",EDGE,"E7");var subQ2=sQuery(id+"F0.wireOp",EDGE,"E6");var subQ3=sQuery(id+"F0.wireOp",EDGE,"E5");var subQ4=sQuery(id+"F0.wireOp",EDGE,"E4");var subQ5=sQuery(id+"F0.wireOp",EDGE,"E1.bottom");var subQ6=sQuery(id+"F0.wireOp",EDGE,"E21.filletArc");var subQ7=sQuery(id+"F0.wireOp",EDGE,"E1.top");var subQ8=sQuery(id+"F0.wireOp",EDGE,"E1.left");var subQ9=sQuery(id+"F0.wireOp",EDGE,"E1.right");var subQ10=sQuery(id+"F0.wireOp",EDGE,"E23.filletArc");var subQ11=sQuery(id+"F0.wireOp",EDGE,"E24.filletArc");Q0=makeQuery(id+"F2.boolean.opBoolean","SPLIT",FACE,{"disambiguationData":[TD([makeQuery(id+"F1.opExtrude","SWEPT_FACE",FACE,{"disambiguationData":[OSD([subQ5])]})])],"derivedFrom":makeQuery(id+"F1.opExtrude","CAP_FACE",FACE,{"disambiguationData":[OSD([subQ5,subQ7,subQ8,subQ9,subQ4,subQ3,subQ2,subQ1,subQ6,subQ0,subQ10,subQ11])],"isStart":true})});}
            var sketch = newSketch(context, id + "F16", { "sketchPlane" : qUnion([Q0])});
            skLineSegment(sketch, "E79", {"start": v(94.05, 208.38) * mm, "end": v(94.05, 238.38) * mm, "construction": true});
            skLineSegment(sketch, "E80", {"start": v(61.05, 208.38) * mm, "end": v(79.05, 226.38) * mm});
            skLineSegment(sketch, "E81", {"start": v(79.05, 226.38) * mm, "end": v(79.05, 238.38) * mm});
            skArc(sketch, "E82", {"start": v(79.05, 238.38) * mm, "mid": v(94.05, 253.38) * mm, "end": v(109.05, 238.38) * mm});
            skLineSegment(sketch, "E83", {"start": v(109.05, 238.38) * mm, "end": v(109.05, 226.38) * mm});
            skLineSegment(sketch, "E84", {"start": v(109.05, 226.38) * mm, "end": v(127.05, 208.38) * mm});
            skCircle(sketch, "E85", {"center": v(94.05, 238.38) * mm, "radius": 6 * mm});
            skLineSegment(sketch, "E86", {"start": v(14.05, 118.38) * mm, "end": v(174.05, 118.38) * mm, "construction": true});
            skLineSegment(sketch, "E87.MirrorCS", {"start": v(109.05, 226.38) * mm, "end": v(109.05, 238.38) * mm});
            skLineSegment(sketch, "E88.MirrorCS", {"start": v(127.05, 208.38) * mm, "end": v(109.05, 226.38) * mm});
            skLineSegment(sketch, "E89.MirrorCS", {"start": v(79.05, 238.38) * mm, "end": v(79.05, 226.38) * mm});
            skLineSegment(sketch, "E90.MirrorCS", {"start": v(79.05, 226.38) * mm, "end": v(61.05, 208.38) * mm});
            skArc(sketch, "E91.MirrorCS", {"start": v(109.05, 238.38) * mm, "mid": v(94.05, 253.38) * mm, "end": v(79.05, 238.38) * mm});
            skLineSegment(sketch, "E92.MirrorCS", {"start": v(174.05, 118.38) * mm, "end": v(14.05, 118.38) * mm, "construction": true});
            skArc(sketch, "E93.MirrorCS", {"start": v(79.05, -1.62) * mm, "mid": v(94.05, -16.62) * mm, "end": v(109.05, -1.62) * mm});
            skArc(sketch, "E94.MirrorCS", {"start": v(109.05, -1.62) * mm, "mid": v(94.05, -16.62) * mm, "end": v(79.05, -1.62) * mm});
            skLineSegment(sketch, "E95.MirrorCS", {"start": v(109.05, -1.62) * mm, "end": v(109.05, 10.38) * mm});
            skLineSegment(sketch, "E96.MirrorCS", {"start": v(109.05, 10.38) * mm, "end": v(127.05, 28.38) * mm});
            skLineSegment(sketch, "E97.MirrorCS", {"start": v(79.05, -1.62) * mm, "end": v(79.05, 10.38) * mm});
            skLineSegment(sketch, "E98.MirrorCS", {"start": v(61.05, 28.38) * mm, "end": v(79.05, 10.38) * mm});
            skCircle(sketch, "E99.MirrorC", {"center": v(94.05, -1.62) * mm, "radius": 6 * mm});
            skLineSegment(sketch, "E100.MirrorCS", {"start": v(109.05, 10.38) * mm, "end": v(109.05, -1.62) * mm});
            skLineSegment(sketch, "E101.MirrorCS", {"start": v(127.05, 28.38) * mm, "end": v(109.05, 10.38) * mm});
            skLineSegment(sketch, "E102.MirrorCS", {"start": v(79.05, 10.38) * mm, "end": v(79.05, -1.62) * mm});
            skLineSegment(sketch, "E103.MirrorCS", {"start": v(79.05, 10.38) * mm, "end": v(61.05, 28.38) * mm});
            skLineSegment(sketch, "E104.MirrorCS", {"start": v(94.05, 28.38) * mm, "end": v(94.05, -1.62) * mm, "construction": true});
            skArc(sketch, "E105.0", {"start": v(24.05, 208.38) * mm, "mid": v(16.98, 205.45) * mm, "end": v(14.05, 198.38) * mm});
            skLineSegment(sketch, "E105.1", {"start": v(14.05, 38.38) * mm, "end": v(14.05, 198.38) * mm});
            skArc(sketch, "E105.2", {"start": v(14.05, 38.38) * mm, "mid": v(16.98, 31.31) * mm, "end": v(24.05, 28.38) * mm});
            skLineSegment(sketch, "E105.3", {"start": v(24.05, 28.38) * mm, "end": v(164.05, 28.38) * mm});
            skArc(sketch, "E105.4", {"start": v(164.05, 28.38) * mm, "mid": v(171.12, 31.31) * mm, "end": v(174.05, 38.38) * mm});
            skLineSegment(sketch, "E105.5", {"start": v(174.05, 38.38) * mm, "end": v(174.05, 198.38) * mm});
            skArc(sketch, "E105.6", {"start": v(174.05, 198.38) * mm, "mid": v(171.12, 205.45) * mm, "end": v(164.05, 208.38) * mm});
            skLineSegment(sketch, "E105.7", {"start": v(24.05, 208.38) * mm, "end": v(164.05, 208.38) * mm});
            skArc(sketch, "E106.0", {"start": v(150.2, 166.56) * mm, "mid": v(94.05, 185.88) * mm, "end": v(37.9, 166.56) * mm});
            skArc(sketch, "E106.1", {"start": v(154.05, 158.68) * mm, "mid": v(153.04, 163.06) * mm, "end": v(150.2, 166.56) * mm});
            skLineSegment(sketch, "E106.2", {"start": v(154.05, 158.68) * mm, "end": v(154.05, 78.09) * mm});
            skArc(sketch, "E106.3", {"start": v(150.2, 70.2) * mm, "mid": v(153.04, 73.7) * mm, "end": v(154.05, 78.09) * mm});
            skArc(sketch, "E106.4", {"start": v(37.9, 70.2) * mm, "mid": v(94.05, 50.88) * mm, "end": v(150.2, 70.2) * mm});
            skArc(sketch, "E106.5", {"start": v(34.05, 78.09) * mm, "mid": v(35.06, 73.7) * mm, "end": v(37.9, 70.2) * mm});
            skArc(sketch, "E106.6", {"start": v(37.9, 166.56) * mm, "mid": v(35.06, 163.06) * mm, "end": v(34.05, 158.68) * mm});
            skLineSegment(sketch, "E106.7", {"start": v(34.05, 158.68) * mm, "end": v(34.05, 78.09) * mm});
            skSolve(sketch);
        }
        {
            var Q0;
            {var subQ9=sQuery(id+"F16.wireOp",EDGE,"E105.0");Q0=makeQuery(id+"F16.imprint","IMPRINT",FACE,{"disambiguationData":[TD([[makeQuery(id+"F16.imprint","IMPRINT",EDGE,{"derivedFrom":subQ9}),1.0]])]});}
            var Q1;
            {var subQ1=sQuery(id+"F16.wireOp",EDGE,"E84");Q1=makeQuery(id+"F16.imprint","IMPRINT",FACE,{"disambiguationData":[TD([[makeQuery(id+"F16.imprint","IMPRINT",EDGE,{"derivedFrom":subQ1}),-1.0]])]});}
            var Q2;
            Q2=makeQuery(id+"F16.imprint","IMPRINT",FACE,{"disambiguationData":[TD([[makeQuery(id+"F16.imprint","IMPRINT",EDGE,{"derivedFrom":sQuery(id+"F16.wireOp",EDGE,"E102.MirrorCS")}),1.0]])]});
            var Q3;
            Q3=makeQuery(id+"F2.opExtrude","CAP_FACE",FACE,{"disambiguationData":[OSD([sQuery(id+"F0.wireOp",EDGE,"E12"),sQuery(id+"F0.wireOp",EDGE,"E13"),sQuery(id+"F0.wireOp",EDGE,"E14"),sQuery(id+"F0.wireOp",EDGE,"E15"),sQuery(id+"F0.wireOp",EDGE,"E17.filletArc"),sQuery(id+"F0.wireOp",EDGE,"E18.filletArc"),sQuery(id+"F0.wireOp",EDGE,"E19.filletArc"),sQuery(id+"F0.wireOp",EDGE,"E20.filletArc"),sQuery(id+"F0.wireOp",EDGE,"E25.0"),sQuery(id+"F0.wireOp",EDGE,"E25.1"),sQuery(id+"F0.wireOp",EDGE,"E25.2"),sQuery(id+"F0.wireOp",EDGE,"E25.3"),sQuery(id+"F0.wireOp",EDGE,"E25.4"),sQuery(id+"F0.wireOp",EDGE,"E25.5"),sQuery(id+"F0.wireOp",EDGE,"E25.6"),sQuery(id+"F0.wireOp",EDGE,"E25.7")])],"isStart":false});
            extrude(context, id + "F17", {"entities" : qUnion([Q0, Q1, Q2]), "endBound" : BoundingType.UP_TO_SURFACE, "endBoundEntityFace" : qUnion([Q3]), "depth" : 25 * mm});
        }
    });
